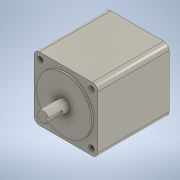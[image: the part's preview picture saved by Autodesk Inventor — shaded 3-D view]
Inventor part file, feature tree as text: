
AUTODESK INVENTOR PART (.ipt)
format: ipt  version: 2022.1 (Build 261234000, 234)  size: 176,128 bytes
history: native  units: in
note: dims shown in document units (in); Inventor stores cm internally (conversion verified against a paired STEP export)
features: extrude x5, sketch x5, fillet x2, chamfer x1
ambient origin geometry x8: Origin, YZ Plane, XZ Plane, XY Plane, X Axis, Y Axis, Z Axis, Center Point
bodies: Solid1 (feature_tree)
feature tree (13):
  extrude  "Extrusion1"  Depth=4.3307in
  extrude  "Extrusion2"  Depth=4.9213in
  extrude  "Extrusion3"  Depth=0.374in
  extrude  "Extrusion4"  Depth=0.1181in TaperAngle=0.0deg
  fillet  "Fillet1"  Radius=3.7402in
  chamfer  "Chamfer1"  Distance=0.1181in
  extrude  "Extrusion5"  Depth=0.1181in TaperAngle=0.0deg
  fillet  "Fillet2"  Radius=0.374in
  sketch  "Sketch1"  dims[d0=4.3307in d1=4.3307in]
  sketch  "Sketch2"  dims[d2=4.8425in d3=0.0in d4=4.9213in]
  sketch  "Sketch3"  dims[d5=45.0deg d6=0.374in]
  sketch  "Sketch4"  dims[d7=1.5748in d9=360.0deg d11=4.8425in d12=0.0in d13=3.7402in d14=0.1181in d15=0.0in]
  sketch  "Sketch5"  dims[d16=0.748in d17=1.4567in d18=0.0in d19=0.374in d20=0.0394in d21=0.0787in d22=45.0deg d23=0.2362in d24=0.2362in d25=0.0in d26=0.8819in d27=0.9843in d28=0.0in d29=0.1181in]
